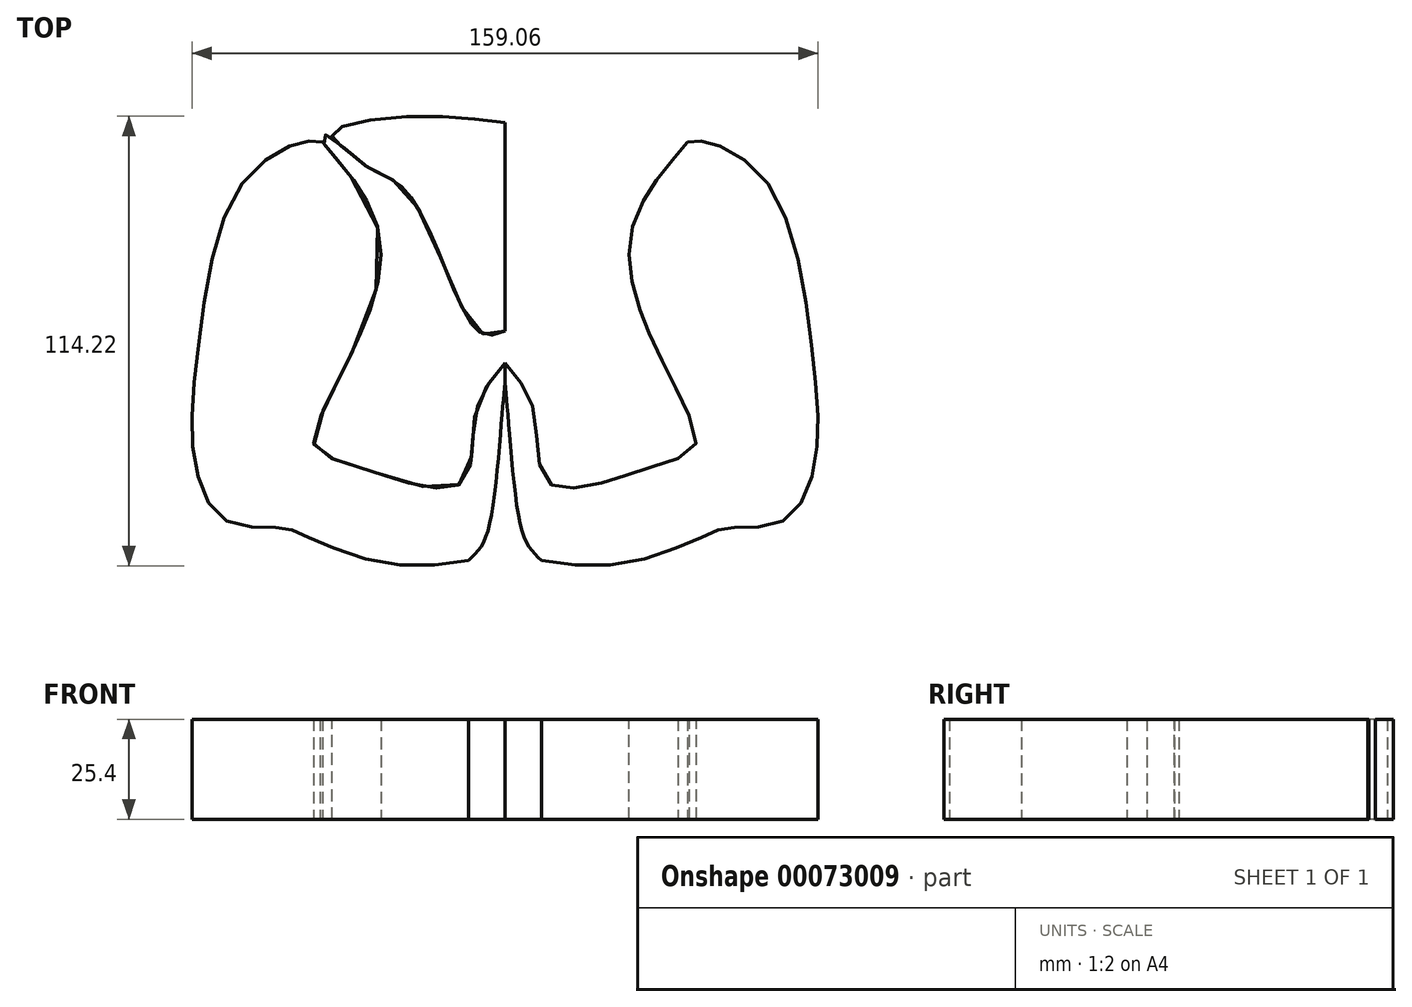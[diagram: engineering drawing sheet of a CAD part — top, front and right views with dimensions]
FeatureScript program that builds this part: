
annotation { "Feature Type Name" : "Feature", "Feature Type Description" : "" }
export const myFeature = defineFeature(function(context is Context, id is Id, definition is map)
    precondition{}
    {
        {
            var Q0;
            Q0=qCreatedBy(makeId("Top.planeOp"),FACE);
            var sketch = newSketch(context, id + "F0", { "sketchPlane" : qUnion([Q0])});
            skFitSpline(sketch, "E0", {"points": [v(0, 5.02) * mm, v(-7.18, 5.35) * mm, v(-24.15, 39.39) * mm, v(-35.82, 47.27) * mm, v(-44.84, 54.69) * mm, v(-46.93, 54.4) * mm, v(-31.64, 27.73) * mm, v(-48.64, -22.6) * mm, v(-39.83, -28.64) * mm, v(-11.47, -33.89) * mm, v(-7.45, -15.66) * mm, v(0, -3.12) * mm], "startDerivative": vector(-137.66, -57.75) * mm, "endDerivative": vector(110.66, 132.38) * mm});
            skLineSegment(sketch, "E1", {"start": v(0, 5.02) * mm, "end": v(0, -3.12) * mm});
            skSolve(sketch);
        }
        {
            var Q0;
            Q0 = qSketchRegion(id + "F0", true);
            extrude(context, id + "F1", {"entities" : qUnion([Q0]), "endBound" : BoundingType.SYMMETRIC, "depth" : 25.4 * mm});
        }
        {
            var Q0;
            Q0=makeQuery(id+"F1.opExtrude","SWEPT_BODY",BODY,{"disambiguationData":[OSD([sQuery(id+"F0.wireOp",EDGE,"E0"),sQuery(id+"F0.wireOp",EDGE,"E1")])]});
            var Q1;
            Q1=qCreatedBy(makeId("Right.planeOp"),FACE);
            mirror(context, id + "F2", {"operationType" : NewBodyOperationType.ADD, "entities" : qUnion([Q0]), "mirrorPlane" : qUnion([Q1])});
        }
        {
            var Q0;
            Q0=qCreatedBy(makeId("Top.planeOp"),FACE);
            var sketch = newSketch(context, id + "F3", { "sketchPlane" : qUnion([Q0])});
            skFitSpline(sketch, "E2", {"points": [v(0, 5.02) * mm, v(-3.58, 3.96) * mm, v(-6.8, 5.02) * mm, v(-8.5, 6.93) * mm, v(-12.32, 14.12) * mm, v(-15.54, 21.78) * mm, v(-19.53, 31.18) * mm, v(-23.02, 37.77) * mm, v(-25.9, 41.36) * mm, v(-29.25, 43.85) * mm, v(-33.15, 45.78) * mm, v(-36.61, 47.84) * mm, v(-40.4, 51.2) * mm, v(-43.84, 54.15) * mm, v(-42.42, 56.43) * mm, v(-21.52, 59.57) * mm, v(0, 58) * mm], "startDerivative": vector(-73.83, -33.45) * mm, "endDerivative": vector(175.51, -22.26) * mm});
            skLineSegment(sketch, "E3", {"start": v(0, 58) * mm, "end": v(0, 5.02) * mm});
            skSolve(sketch);
        }
        {
            var Q0;
            Q0 = qSketchRegion(id + "F3", true);
            extrude(context, id + "F4", {"entities" : qUnion([Q0]), "endBound" : BoundingType.SYMMETRIC, "depth" : 25.4 * mm});
        }
        {
            var Q0;
            Q0=makeQuery(id+"F4.opExtrude","SWEPT_BODY",BODY,{"disambiguationData":[OSD([sQuery(id+"F3.wireOp",EDGE,"E2"),sQuery(id+"F3.wireOp",EDGE,"E3")])]});
            var Q1;
            Q1=qCreatedBy(makeId("Right.planeOp"),FACE);
            mirror(context, id + "F5", {"entities" : qUnion([Q0]), "mirrorPlane" : qUnion([Q1])});
        }
        {
            var Q0;
            Q0=qCreatedBy(makeId("Top.planeOp"),FACE);
            var sketch = newSketch(context, id + "F6", { "sketchPlane" : qUnion([Q0])});
            skFitSpline(sketch, "E4", {"points": [v(0, -3.12) * mm, v(-2.73, -6.38) * mm, v(-4.93, -9.43) * mm, v(-6.75, -13.17) * mm, v(-7.87, -18.61) * mm, v(-8.2, -24.12) * mm, v(-8.83, -29.3) * mm, v(-10.34, -32.82) * mm, v(-12.96, -34.59) * mm, v(-15.9, -35) * mm, v(-20.4, -34.55) * mm, v(-25.38, -33.37) * mm, v(-29.25, -32.2) * mm, v(-32.69, -31.05) * mm, v(-37.8, -29.3) * mm, v(-42.28, -27.88) * mm, v(-46.65, -26.19) * mm, v(-48.58, -23.6) * mm, v(-47.76, -18.94) * mm, v(-45.4, -13.57) * mm, v(-42.95, -8.66) * mm, v(-40.16, -3.12) * mm, v(-37.4, 2.71) * mm, v(-35.84, 6.35) * mm, v(-34.43, 10.03) * mm, v(-32.78, 15.37) * mm, v(-31.8, 20.23) * mm, v(-31.47, 24.79) * mm, v(-31.98, 29.78) * mm, v(-33.42, 34.48) * mm, v(-35.57, 38.89) * mm, v(-37.23, 41.58) * mm, v(-40.23, 45.67) * mm, v(-43.4, 49.48) * mm, v(-45.52, 51.98) * mm, v(-46.32, 53.03) * mm], "startDerivative": vector(-99.78, -118.38) * mm, "endDerivative": vector(-46.25, 60.57) * mm});
            skFitSpline(sketch, "E5", {"points": [v(-46.32, 53.03) * mm, v(-51.52, 53.03) * mm, v(-67.42, 41.51) * mm, v(-78.02, 0) * mm, v(-79.02, -26.74) * mm, v(-71.07, -42.98) * mm, v(-57.15, -44.97) * mm, v(-50.85, -46.96) * mm, v(-28.66, -54.25) * mm, v(0, -51.26) * mm], "startDerivative": vector(-77.31, 12.22) * mm, "endDerivative": vector(208.16, 46.87) * mm});
            skFitSpline(sketch, "E6", {"points": [v(-9.25, -53.23) * mm, v(-6.37, -50.2) * mm, v(-3.51, -42.26) * mm, v(-0.78, -16.68) * mm, v(0, -8.11) * mm], "startDerivative": vector(19.27, 17.32) * mm, "endDerivative": vector(3, 30.47) * mm});
            skLineSegment(sketch, "E7", {"start": v(0, -3.12) * mm, "end": v(0, -8.11) * mm});
            skSolve(sketch);
        }
        {
            var Q0;
            Q0 = qSketchRegion(id + "F6", true);
            extrude(context, id + "F7", {"entities" : qUnion([Q0]), "endBound" : BoundingType.SYMMETRIC, "depth" : 25.4 * mm});
        }
        {
            var Q0;
            Q0=makeQuery(id+"F7.opExtrude","SWEPT_BODY",BODY,{"disambiguationData":[OSD([sQuery(id+"F6.wireOp",EDGE,"E4"),sQuery(id+"F6.wireOp",EDGE,"E5"),sQuery(id+"F6.wireOp",EDGE,"9oo3a5aO-wlWv-dHfE-YGEc-IfWzUgmbNUcP")])]});
            var Q1;
            Q1=qCreatedBy(makeId("Right.planeOp"),FACE);
            mirror(context, id + "F8", {"entities" : qUnion([Q0]), "mirrorPlane" : qUnion([Q1])});
        }
    });
